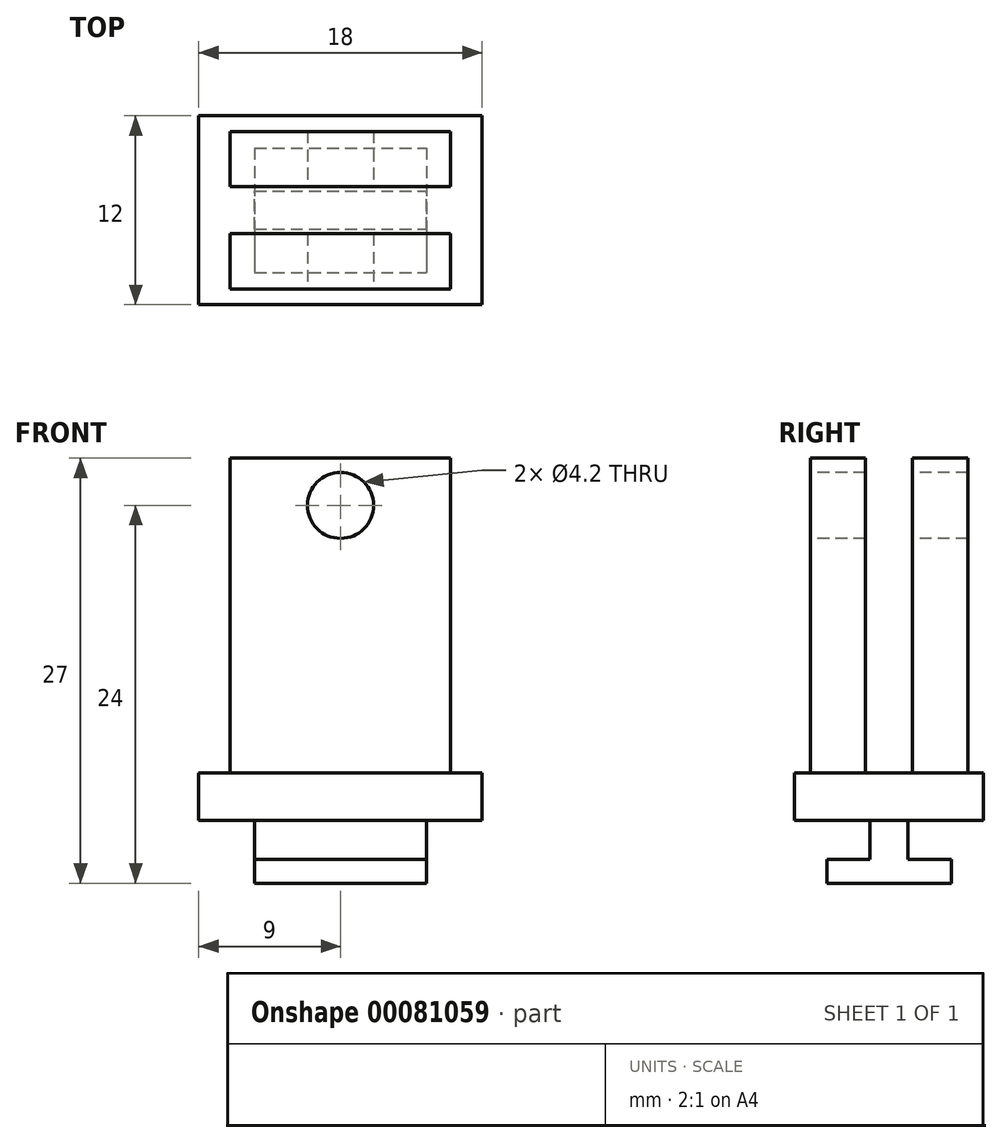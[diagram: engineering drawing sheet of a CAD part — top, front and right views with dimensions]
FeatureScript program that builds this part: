
annotation { "Feature Type Name" : "Feature", "Feature Type Description" : "" }
export const myFeature = defineFeature(function(context is Context, id is Id, definition is map)
    precondition{}
    {
        {
            var Q0;
            Q0=qCreatedBy(makeId("Top.planeOp"),FACE);
            var sketch = newSketch(context, id + "F0", { "sketchPlane" : qUnion([Q0])});
            skLineSegment(sketch, "E0.bottom", {"start": v(-9, 6) * mm, "end": v(9, 6) * mm});
            skLineSegment(sketch, "E0.top", {"start": v(-9, -6) * mm, "end": v(9, -6) * mm});
            skLineSegment(sketch, "E0.left", {"start": v(-9, 6) * mm, "end": v(-9, -6) * mm});
            skLineSegment(sketch, "E0.right", {"start": v(9, 6) * mm, "end": v(9, -6) * mm});
            skPoint(sketch, "E0.middle", {"position": v(0, 0) * mm});
            skSolve(sketch);
        }
        {
            var Q0;
            Q0=makeQuery(id+"F0.imprint","IMPRINT",FACE,{"disambiguationData":[TD([[makeQuery(id+"F0.imprint","IMPRINT",EDGE,{"derivedFrom":sQuery(id+"F0.wireOp",EDGE,"E0.bottom")}),-1.0]])]});
            extrude(context, id + "F1", {"entities" : qUnion([Q0]), "endBound" : BoundingType.SYMMETRIC, "depth" : 3 * mm});
        }
        {
            var Q0;
            Q0=makeQuery(id+"F1.opExtrude","CAP_FACE",FACE,{"disambiguationData":[OSD([sQuery(id+"F0.wireOp",EDGE,"E0.bottom"),sQuery(id+"F0.wireOp",EDGE,"E0.top"),sQuery(id+"F0.wireOp",EDGE,"E0.left"),sQuery(id+"F0.wireOp",EDGE,"E0.right")])],"isStart":false});
            var sketch = newSketch(context, id + "F2", { "sketchPlane" : qUnion([Q0])});
            skLineSegment(sketch, "E1.bottom", {"start": v(-7, 5) * mm, "end": v(7, 5) * mm});
            skLineSegment(sketch, "E1.top", {"start": v(-7, -5) * mm, "end": v(7, -5) * mm});
            skLineSegment(sketch, "E1.left", {"start": v(-7, 5) * mm, "end": v(-7, -5) * mm});
            skLineSegment(sketch, "E1.right", {"start": v(7, 5) * mm, "end": v(7, -5) * mm});
            skPoint(sketch, "E1.middle", {"position": v(0, 0) * mm});
            skSolve(sketch);
        }
        {
            var Q0;
            Q0=makeQuery(id+"F2.imprint","IMPRINT",FACE,{"disambiguationData":[TD([[makeQuery(id+"F2.imprint","IMPRINT",EDGE,{"derivedFrom":sQuery(id+"F2.wireOp",EDGE,"E1.bottom")}),-1.0]])]});
            extrude(context, id + "F3", {"entities" : qUnion([Q0]), "operationType" : NewBodyOperationType.ADD, "depth" : 20 * mm});
        }
        {
            var Q0;
            Q0=makeQuery(id+"F3.opExtrude","SWEPT_FACE",FACE,{"disambiguationData":[OSD([sQuery(id+"F2.wireOp",EDGE,"E1.right")])]});
            var sketch = newSketch(context, id + "F4", { "sketchPlane" : qUnion([Q0])});
            skLineSegment(sketch, "E2.bottom", {"start": v(1.5, 1.5) * mm, "end": v(-1.5, 1.5) * mm});
            skLineSegment(sketch, "E2.top", {"start": v(1.5, 21.5) * mm, "end": v(-1.5, 21.5) * mm});
            skLineSegment(sketch, "E2.left", {"start": v(1.5, 1.5) * mm, "end": v(1.5, 21.5) * mm});
            skLineSegment(sketch, "E2.right", {"start": v(-1.5, 1.5) * mm, "end": v(-1.5, 21.5) * mm});
            skSolve(sketch);
        }
        {
            var Q0;
            Q0=makeQuery(id+"F4.imprint","IMPRINT",FACE,{"disambiguationData":[TD([[makeQuery(id+"F4.imprint","IMPRINT",EDGE,{"derivedFrom":sQuery(id+"F4.wireOp",EDGE,"E2.bottom")}),-1.0]])]});
            extrude(context, id + "F5", {"entities" : qUnion([Q0]), "operationType" : NewBodyOperationType.REMOVE, "oppositeDirection" : true, "depth" : 25 * mm});
        }
        {
            var Q0;
            Q0=makeQuery(id+"F3.opExtrude","SWEPT_FACE",FACE,{"disambiguationData":[OSD([sQuery(id+"F2.wireOp",EDGE,"E1.top")])]});
            var sketch = newSketch(context, id + "F6", { "sketchPlane" : qUnion([Q0])});
            skPoint(sketch, "E3", {"position": v(0, 18.5) * mm});
            skSolve(sketch);
        }
        {
            var Q0;
            Q0=sQuery(id+"F6.wireOp",VERTEX,"E3");
            var Q1;
            Q1=makeQuery(id+"F1.opExtrude","SWEPT_BODY",BODY,{"disambiguationData":[OSD([sQuery(id+"F0.wireOp",EDGE,"E0.bottom"),sQuery(id+"F0.wireOp",EDGE,"E0.top"),sQuery(id+"F0.wireOp",EDGE,"E0.left"),sQuery(id+"F0.wireOp",EDGE,"E0.right")])]});
            hole(context, id + "F7", {"style" : HoleStyle.SIMPLE, "endStyle" : HoleEndStyle.THROUGH, "holeDiameter" : 4.2 * mm, "locations" : qUnion([Q0]), "scope" : qUnion([Q1]), "isTappedThrough" : true});
        }
        {
            var Q0;
            Q0=makeQuery(id+"F1.opExtrude","CAP_FACE",FACE,{"disambiguationData":[OSD([sQuery(id+"F0.wireOp",EDGE,"E0.bottom"),sQuery(id+"F0.wireOp",EDGE,"E0.top"),sQuery(id+"F0.wireOp",EDGE,"E0.left"),sQuery(id+"F0.wireOp",EDGE,"E0.right")])],"isStart":true});
            var sketch = newSketch(context, id + "F8", { "sketchPlane" : qUnion([Q0])});
            skLineSegment(sketch, "E4.bottom", {"start": v(-5.45, 1.2) * mm, "end": v(5.45, 1.2) * mm});
            skLineSegment(sketch, "E4.top", {"start": v(-5.45, -1.2) * mm, "end": v(5.45, -1.2) * mm});
            skLineSegment(sketch, "E4.left", {"start": v(-5.45, 1.2) * mm, "end": v(-5.45, -1.2) * mm});
            skLineSegment(sketch, "E4.right", {"start": v(5.45, 1.2) * mm, "end": v(5.45, -1.2) * mm});
            skPoint(sketch, "E4.middle", {"position": v(0, 0) * mm});
            skSolve(sketch);
        }
        {
            var Q0;
            Q0=makeQuery(id+"F8.imprint","IMPRINT",FACE,{"disambiguationData":[TD([[makeQuery(id+"F8.imprint","IMPRINT",EDGE,{"derivedFrom":sQuery(id+"F8.wireOp",EDGE,"E4.bottom")}),-1.0]])]});
            extrude(context, id + "F9", {"entities" : qUnion([Q0]), "operationType" : NewBodyOperationType.ADD, "depth" : 2.5 * mm});
        }
        {
            var Q0;
            Q0=makeQuery(id+"F9.opExtrude","CAP_FACE",FACE,{"disambiguationData":[OSD([sQuery(id+"F8.wireOp",EDGE,"E4.bottom"),sQuery(id+"F8.wireOp",EDGE,"E4.top"),sQuery(id+"F8.wireOp",EDGE,"E4.left"),sQuery(id+"F8.wireOp",EDGE,"E4.right")])],"isStart":false});
            var sketch = newSketch(context, id + "F10", { "sketchPlane" : qUnion([Q0])});
            skLineSegment(sketch, "E5.bottom", {"start": v(-5.45, -3.95) * mm, "end": v(5.45, -3.95) * mm});
            skLineSegment(sketch, "E5.top", {"start": v(-5.45, 3.95) * mm, "end": v(5.45, 3.95) * mm});
            skLineSegment(sketch, "E5.left", {"start": v(-5.45, -3.95) * mm, "end": v(-5.45, 3.95) * mm});
            skLineSegment(sketch, "E5.right", {"start": v(5.45, -3.95) * mm, "end": v(5.45, 3.95) * mm});
            skPoint(sketch, "E5.middle", {"position": v(0, 0) * mm});
            skSolve(sketch);
        }
        {
            var Q0;
            {var subQ0=sQuery(id+"F10.wireOp",EDGE,"E5.bottom");Q0=makeQuery(id+"F10.imprint","IMPRINT",FACE,{"disambiguationData":[TD([[makeQuery(id+"F10.imprint","IMPRINT",EDGE,{"derivedFrom":subQ0}),1.0]])]});}
            var Q1;
            {var subQ1=makeQuery(id+"F9.opExtrude","CAP_EDGE",EDGE,{"disambiguationData":[OSD([sQuery(id+"F8.wireOp",EDGE,"E4.bottom")])],"isStart":false});Q1=makeQuery(id+"F10.imprint","IMPRINT",FACE,{"disambiguationData":[TD([[makeQuery(id+"F10.imprint","IMPRINT",EDGE,{"derivedFrom":subQ1}),-1.0]])]});}
            var Q2;
            {var subQ0=sQuery(id+"F10.wireOp",EDGE,"E5.top");Q2=makeQuery(id+"F10.imprint","IMPRINT",FACE,{"disambiguationData":[TD([[makeQuery(id+"F10.imprint","IMPRINT",EDGE,{"derivedFrom":subQ0}),-1.0]])]});}
            extrude(context, id + "F11", {"entities" : qUnion([Q0, Q1, Q2]), "operationType" : NewBodyOperationType.ADD, "depth" : 1.5 * mm});
        }
    });
